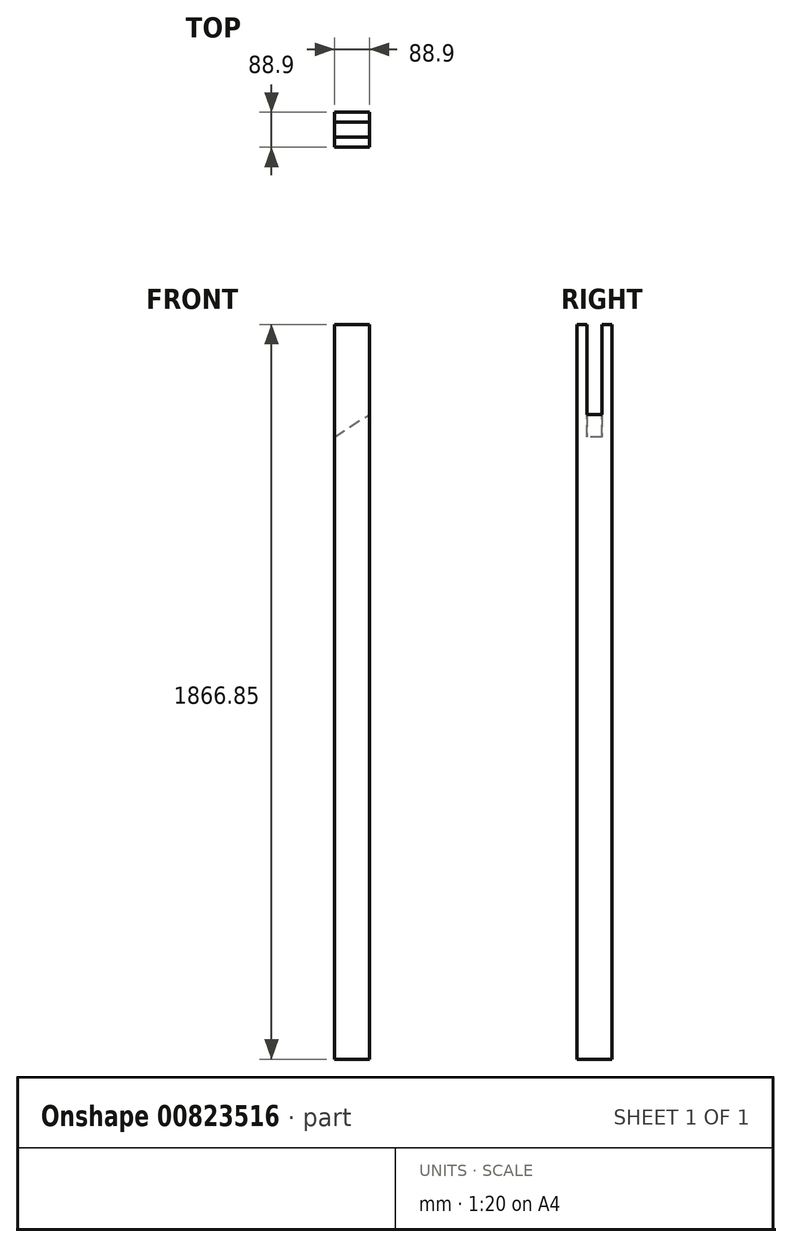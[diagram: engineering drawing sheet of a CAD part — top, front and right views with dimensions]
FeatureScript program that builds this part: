
annotation { "Feature Type Name" : "Feature", "Feature Type Description" : "" }
export const myFeature = defineFeature(function(context is Context, id is Id, definition is map)
    precondition{}
    {
        {
            var Q0;
            Q0=qCreatedBy(makeId("Top.planeOp"),FACE);
            var sketch = newSketch(context, id + "F0", { "sketchPlane" : qUnion([Q0])});
            skLineSegment(sketch, "E0.bottom", {"start": v(-44.45, -44.45) * mm, "end": v(44.45, -44.45) * mm});
            skLineSegment(sketch, "E0.top", {"start": v(-44.45, 44.45) * mm, "end": v(44.45, 44.45) * mm});
            skLineSegment(sketch, "E0.left", {"start": v(-44.45, -44.45) * mm, "end": v(-44.45, 44.45) * mm});
            skLineSegment(sketch, "E0.right", {"start": v(44.45, -44.45) * mm, "end": v(44.45, 44.45) * mm});
            skSolve(sketch);
        }
        {
            var Q0;
            Q0 = qSketchRegion(id + "F0", true);
            extrude(context, id + "F1", {"entities" : qUnion([Q0]), "depth" : 1866.85 * mm, "offsetDistance" : 25.4 * mm});
        }
        {
            var Q0;
            Q0=qCreatedBy(makeId("Front.planeOp"),FACE);
            var sketch = newSketch(context, id + "F2", { "sketchPlane" : qUnion([Q0])});
            skLineSegment(sketch, "E1", {"start": v(44.45, 1866.85) * mm, "end": v(-44.45, 1866.85) * mm});
            skLineSegment(sketch, "E2", {"start": v(-44.45, 1866.85) * mm, "end": v(-44.45, 1581.07) * mm});
            skLineSegment(sketch, "E3", {"start": v(-44.45, 1581.07) * mm, "end": v(44.45, 1638.25) * mm});
            skLineSegment(sketch, "E4", {"start": v(44.45, 1638.25) * mm, "end": v(44.45, 1866.85) * mm});
            skSolve(sketch);
        }
        {
            var Q0;
            Q0 = qSketchRegion(id + "F2", true);
            extrude(context, id + "F3", {"entities" : qUnion([Q0]), "operationType" : NewBodyOperationType.REMOVE, "endBound" : BoundingType.SYMMETRIC, "oppositeDirection" : true, "depth" : 38.1 * mm, "offsetDistance" : 25.4 * mm});
        }
    });
